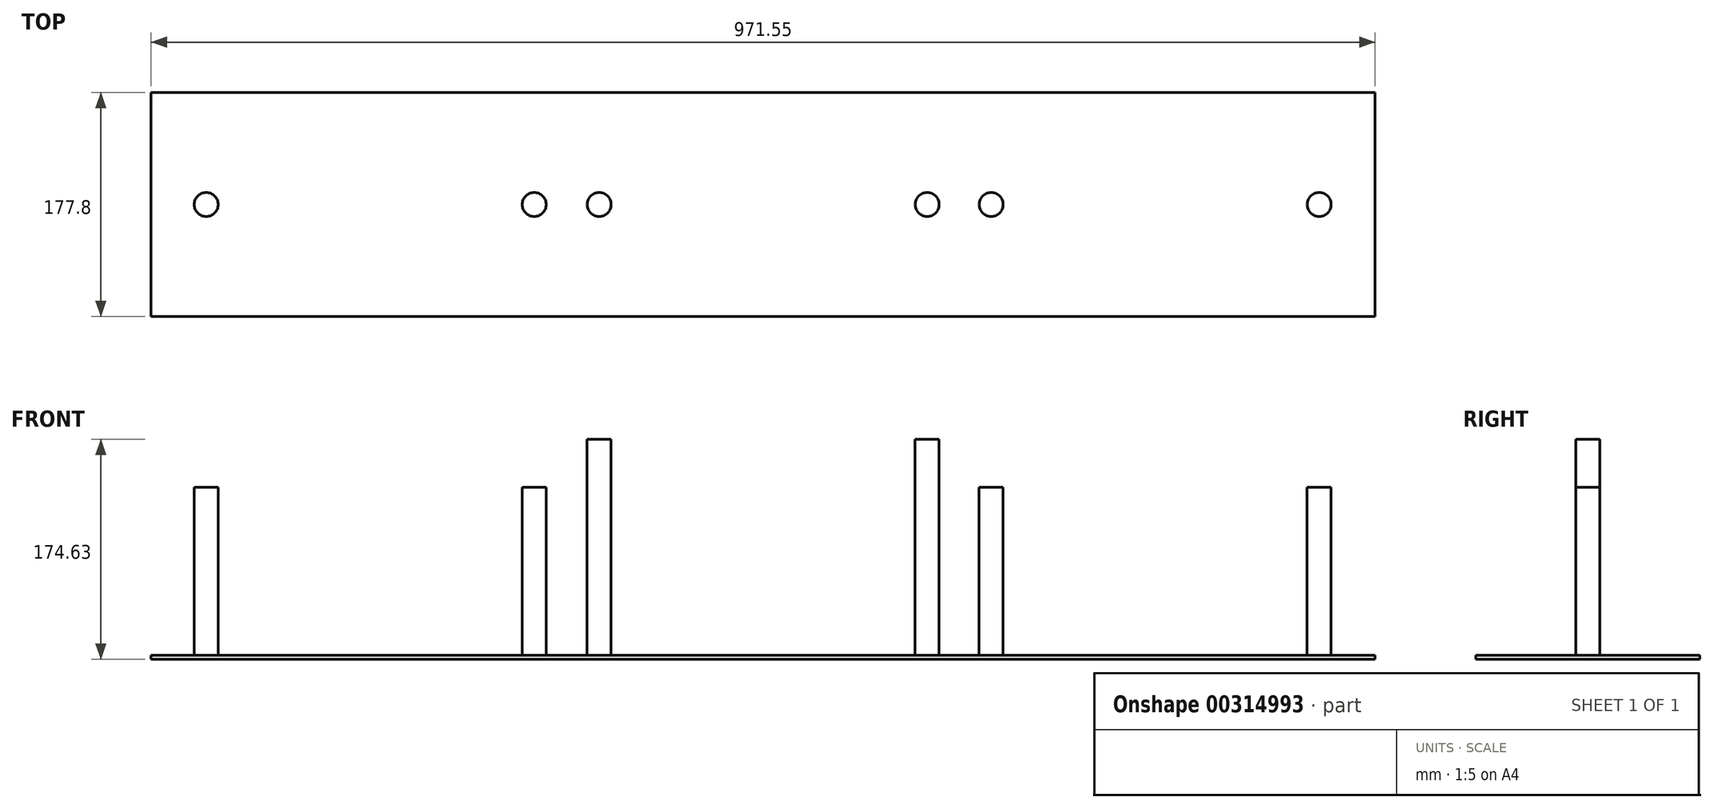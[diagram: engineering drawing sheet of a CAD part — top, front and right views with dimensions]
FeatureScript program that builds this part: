
annotation { "Feature Type Name" : "Feature", "Feature Type Description" : "" }
export const myFeature = defineFeature(function(context is Context, id is Id, definition is map)
    precondition{}
    {
        {
            var Q0;
            Q0=qCreatedBy(makeId("Top.planeOp"),FACE);
            var sketch = newSketch(context, id + "F0", { "sketchPlane" : qUnion([Q0])});
            skLineSegment(sketch, "E0.bottom", {"start": v(0, 0) * mm, "end": v(971.55, 0) * mm});
            skLineSegment(sketch, "E0.top", {"start": v(0, -177.8) * mm, "end": v(971.55, -177.8) * mm});
            skLineSegment(sketch, "E0.left", {"start": v(0, 0) * mm, "end": v(0, -177.8) * mm});
            skLineSegment(sketch, "E0.right", {"start": v(971.55, 0) * mm, "end": v(971.55, -177.8) * mm});
            skSolve(sketch);
        }
        {
            var Q0;
            Q0 = qSketchRegion(id + "F0", true);
            extrude(context, id + "F1", {"entities" : qUnion([Q0]), "depth" : 3.17 * mm});
        }
        {
            var Q0;
            Q0=makeQuery(id+"F1.opExtrude","CAP_FACE",FACE,{"disambiguationData":[OSD([sQuery(id+"F0.wireOp",EDGE,"E0.bottom"),sQuery(id+"F0.wireOp",EDGE,"E0.top"),sQuery(id+"F0.wireOp",EDGE,"E0.left"),sQuery(id+"F0.wireOp",EDGE,"E0.right")])],"isStart":false});
            var sketch = newSketch(context, id + "F2", { "sketchPlane" : qUnion([Q0])});
            skPoint(sketch, "E1.1", {"position": v(0, 0) * mm});
            skLineSegment(sketch, "E1.2.0", {"start": v(0, 0) * mm, "end": v(0, -177.8) * mm});
            skLineSegment(sketch, "E1.2.2", {"start": v(0, -177.8) * mm, "end": v(0, 0) * mm});
            skLineSegment(sketch, "E1.4.0", {"start": v(0, -177.8) * mm, "end": v(971.55, -177.8) * mm});
            skLineSegment(sketch, "E1.4.2", {"start": v(971.55, -177.8) * mm, "end": v(0, -177.8) * mm});
            skPoint(sketch, "E1.5", {"position": v(0, 0) * mm});
            skLineSegment(sketch, "E1.7.0", {"start": v(0, 0) * mm, "end": v(0, -177.8) * mm});
            skLineSegment(sketch, "E1.7.1", {"start": v(0, -177.8) * mm, "end": v(971.55, -177.8) * mm});
            skLineSegment(sketch, "E1.7.2", {"start": v(971.55, -177.8) * mm, "end": v(971.55, 0) * mm});
            skLineSegment(sketch, "E1.7.3", {"start": v(971.55, 0) * mm, "end": v(0, 0) * mm});
            skLineSegment(sketch, "E1.9", {"start": v(971.55, 0) * mm, "end": v(971.55, -177.8) * mm});
            skPoint(sketch, "E1.10", {"position": v(971.55, -177.8) * mm});
            skLineSegment(sketch, "E1.11", {"start": v(971.55, 0) * mm, "end": v(971.55, -177.8) * mm});
            skPoint(sketch, "E1.12", {"position": v(0, 0) * mm});
            skLineSegment(sketch, "E1.13.0", {"start": v(0, -177.8) * mm, "end": v(0, 0) * mm});
            skLineSegment(sketch, "E1.13.1", {"start": v(0, 0) * mm, "end": v(971.55, 0) * mm});
            skLineSegment(sketch, "E1.13.2", {"start": v(971.55, 0) * mm, "end": v(971.55, -177.8) * mm});
            skLineSegment(sketch, "E1.13.3", {"start": v(971.55, -177.8) * mm, "end": v(0, -177.8) * mm});
            skPoint(sketch, "E1.14", {"position": v(0, -177.8) * mm});
            skLineSegment(sketch, "E1.15.0", {"start": v(971.55, 0) * mm, "end": v(0, 0) * mm});
            skLineSegment(sketch, "E1.15.2", {"start": v(0, 0) * mm, "end": v(971.55, 0) * mm});
            skLineSegment(sketch, "E1.16", {"start": v(0, 0) * mm, "end": v(0, -177.8) * mm});
            skLineSegment(sketch, "E1.17", {"start": v(0, -177.8) * mm, "end": v(971.55, -177.8) * mm});
            skPoint(sketch, "E1.18", {"position": v(0, -177.8) * mm});
            skPoint(sketch, "E1.19", {"position": v(971.55, -177.8) * mm});
            skLineSegment(sketch, "E1.20", {"start": v(0, 0) * mm, "end": v(0, -177.8) * mm});
            skLineSegment(sketch, "E1.21", {"start": v(0, 0) * mm, "end": v(971.55, 0) * mm});
            skPoint(sketch, "E1.22", {"position": v(971.55, 0) * mm});
            skLineSegment(sketch, "E1.23", {"start": v(0, -177.8) * mm, "end": v(971.55, -177.8) * mm});
            skLineSegment(sketch, "E1.24", {"start": v(0, 0) * mm, "end": v(971.55, 0) * mm});
            skPoint(sketch, "E1.25", {"position": v(971.55, 0) * mm});
            skLineSegment(sketch, "E1.26.0", {"start": v(971.55, -177.8) * mm, "end": v(971.55, 0) * mm});
            skLineSegment(sketch, "E1.26.2", {"start": v(971.55, 0) * mm, "end": v(971.55, -177.8) * mm});
            skLineSegment(sketch, "E2", {"start": v(0, -88.9) * mm, "end": v(971.55, -88.9) * mm, "construction": true});
            skCircle(sketch, "E3", {"center": v(43.69, -88.9) * mm, "radius": 9.52 * mm});
            skCircle(sketch, "E4", {"center": v(304.04, -88.9) * mm, "radius": 9.52 * mm});
            skCircle(sketch, "E5", {"center": v(355.6, -88.9) * mm, "radius": 9.52 * mm});
            skCircle(sketch, "E6", {"center": v(615.95, -88.9) * mm, "radius": 9.52 * mm});
            skCircle(sketch, "E7", {"center": v(927.1, -88.9) * mm, "radius": 9.52 * mm});
            skCircle(sketch, "E8", {"center": v(666.75, -88.9) * mm, "radius": 9.52 * mm});
            skLineSegment(sketch, "E9", {"start": v(43.69, -88.9) * mm, "end": v(304.04, -88.9) * mm});
            skLineSegment(sketch, "E10", {"start": v(355.6, -88.9) * mm, "end": v(615.95, -88.9) * mm});
            skLineSegment(sketch, "E11", {"start": v(666.75, -88.9) * mm, "end": v(927.1, -88.9) * mm});
            skLineSegment(sketch, "E12", {"start": v(485.78, 0) * mm, "end": v(485.78, -88.9) * mm, "construction": true});
            skSolve(sketch);
        }
        {
            var Q0;
            Q0=makeQuery(id+"F2.imprint","IMPRINT",FACE,{"disambiguationData":[TD([[makeQuery(id+"F2.imprint","IMPRINT",EDGE,{"derivedFrom":sQuery(id+"F2.wireOp",EDGE,"E3")}),1.0]])]});
            var Q1;
            Q1=makeQuery(id+"F2.imprint","IMPRINT",FACE,{"disambiguationData":[TD([[makeQuery(id+"F2.imprint","IMPRINT",EDGE,{"derivedFrom":sQuery(id+"F2.wireOp",EDGE,"E4")}),1.0]])]});
            var Q2;
            Q2=makeQuery(id+"F2.imprint","IMPRINT",FACE,{"disambiguationData":[TD([[makeQuery(id+"F2.imprint","IMPRINT",EDGE,{"derivedFrom":sQuery(id+"F2.wireOp",EDGE,"E5")}),1.0]])]});
            var Q3;
            Q3=makeQuery(id+"F2.imprint","IMPRINT",FACE,{"disambiguationData":[TD([[makeQuery(id+"F2.imprint","IMPRINT",EDGE,{"derivedFrom":sQuery(id+"F2.wireOp",EDGE,"E6")}),1.0]])]});
            var Q4;
            Q4=makeQuery(id+"F2.imprint","IMPRINT",FACE,{"disambiguationData":[TD([[makeQuery(id+"F2.imprint","IMPRINT",EDGE,{"derivedFrom":sQuery(id+"F2.wireOp",EDGE,"E8")}),1.0]])]});
            var Q5;
            Q5=makeQuery(id+"F2.imprint","IMPRINT",FACE,{"disambiguationData":[TD([[makeQuery(id+"F2.imprint","IMPRINT",EDGE,{"derivedFrom":sQuery(id+"F2.wireOp",EDGE,"E7")}),1.0]])]});
            extrude(context, id + "F3", {"entities" : qUnion([Q0, Q1, Q2, Q3, Q4, Q5]), "operationType" : NewBodyOperationType.ADD, "depth" : 133.35 * mm});
        }
        {
            var Q0;
            Q0=makeQuery(id+"F3.opExtrude","CAP_FACE",FACE,{"disambiguationData":[OSD([sQuery(id+"F2.wireOp",EDGE,"E5")])],"isStart":false});
            var Q1;
            Q1=makeQuery(id+"F3.opExtrude","CAP_FACE",FACE,{"disambiguationData":[OSD([sQuery(id+"F2.wireOp",EDGE,"E6")])],"isStart":false});
            extrude(context, id + "F4", {"entities" : qUnion([Q0, Q1]), "operationType" : NewBodyOperationType.ADD, "depth" : 38.1 * mm});
        }
    });
